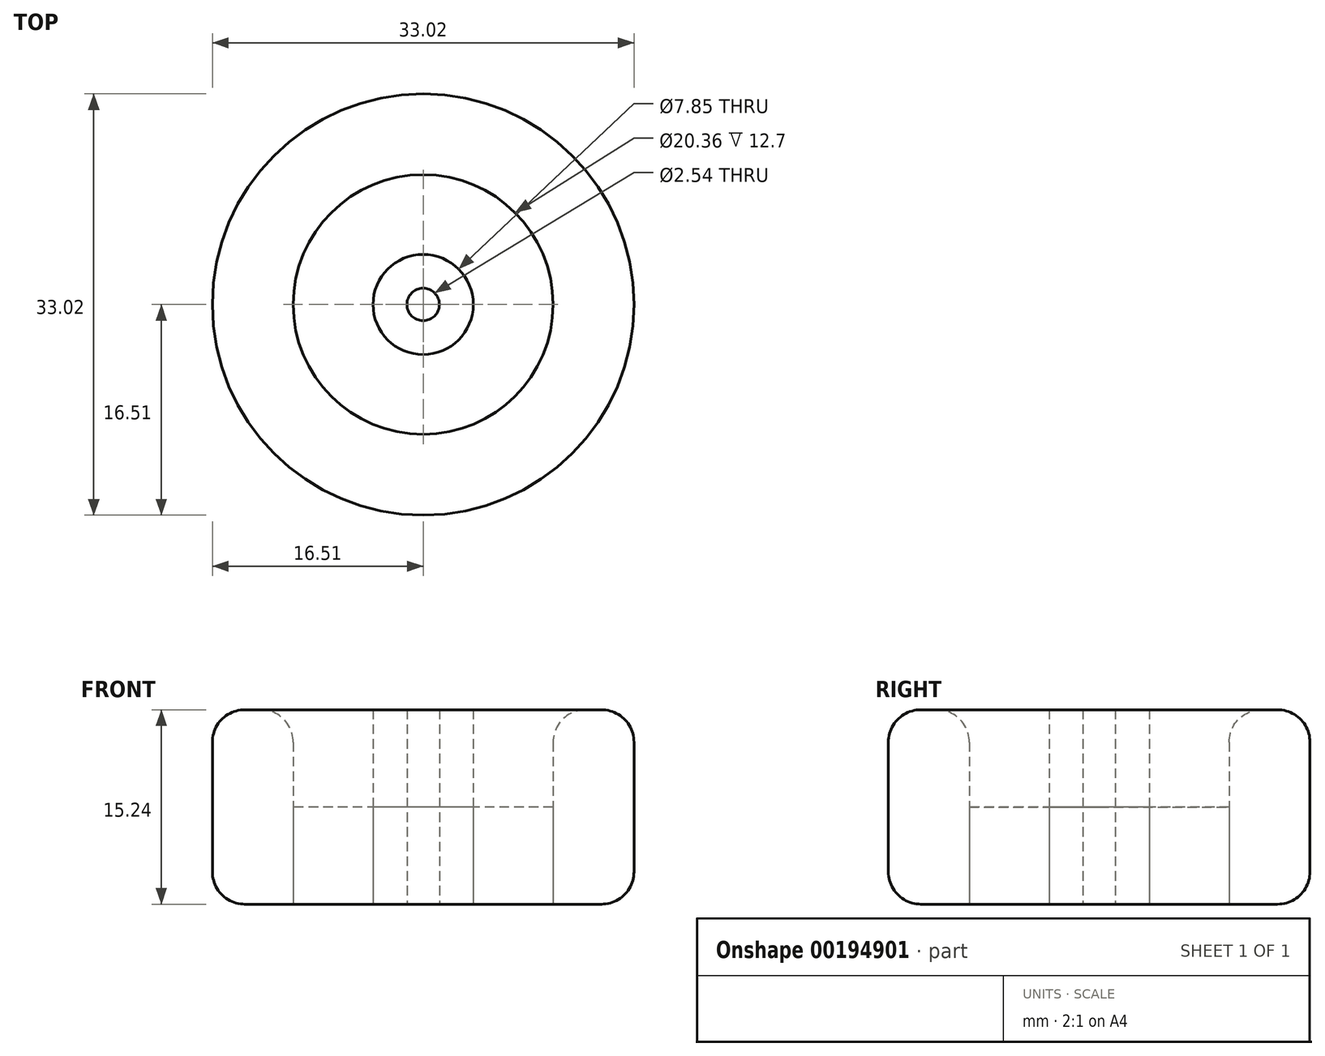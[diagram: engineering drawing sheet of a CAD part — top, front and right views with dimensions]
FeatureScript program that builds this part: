
annotation { "Feature Type Name" : "Feature", "Feature Type Description" : "" }
export const myFeature = defineFeature(function(context is Context, id is Id, definition is map)
    precondition{}
    {
        {
            var Q0;
            Q0=qCreatedBy(makeId("Top.planeOp"),FACE);
            var sketch = newSketch(context, id + "F0", { "sketchPlane" : qUnion([Q0])});
            skCircle(sketch, "E0", {"center": v(0, 0) * mm, "radius": 16.51 * mm});
            skCircle(sketch, "E1", {"center": v(0, 0) * mm, "radius": 1.27 * mm});
            skCircle(sketch, "E2", {"center": v(0, 0) * mm, "radius": 3.93 * mm});
            skCircle(sketch, "E3", {"center": v(0, 0) * mm, "radius": 10.18 * mm});
            skSolve(sketch);
        }
        {
            var Q0;
            Q0=makeQuery(id+"F0.imprint","IMPRINT",FACE,{"disambiguationData":[TD([[makeQuery(id+"F0.imprint","IMPRINT",EDGE,{"derivedFrom":sQuery(id+"F0.wireOp",EDGE,"E0")}),1.0]])]});
            var Q1;
            Q1=makeQuery(id+"F0.imprint","IMPRINT",FACE,{"disambiguationData":[TD([[makeQuery(id+"F0.imprint","IMPRINT",EDGE,{"derivedFrom":sQuery(id+"F0.wireOp",EDGE,"E1")}),-1.0]])]});
            extrude(context, id + "F1", {"entities" : qUnion([Q0, Q1]), "depth" : 15.24 * mm});
        }
        {
            var Q0;
            Q0=makeQuery(id+"F0.imprint","IMPRINT",FACE,{"disambiguationData":[TD([[makeQuery(id+"F0.imprint","IMPRINT",EDGE,{"derivedFrom":sQuery(id+"F0.wireOp",EDGE,"E2")}),-1.0]])]});
            extrude(context, id + "F2", {"entities" : qUnion([Q0]), "depth" : 7.62 * mm});
        }
        {
            var Q0;
            Q0=makeQuery(id+"F1.opExtrude","CAP_EDGE",EDGE,{"disambiguationData":[OSD([sQuery(id+"F0.wireOp",EDGE,"E0")])],"isStart":false});
            var Q1;
            Q1=makeQuery(id+"F1.opExtrude","CAP_EDGE",EDGE,{"disambiguationData":[OSD([sQuery(id+"F0.wireOp",EDGE,"E0")])],"isStart":true});
            var Q2;
            Q2=makeQuery(id+"F1.opExtrude","CAP_EDGE",EDGE,{"disambiguationData":[OSD([sQuery(id+"F0.wireOp",EDGE,"E3")])],"isStart":false});
            fillet(context, id + "F3", {"entities" : qUnion([Q0, Q1, Q2]), "radius" : 2.54 * mm, "tangentPropagation" : true, "allowEdgeOverflow" : false});
        }
    });
